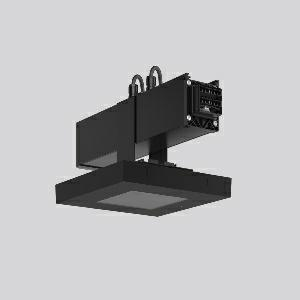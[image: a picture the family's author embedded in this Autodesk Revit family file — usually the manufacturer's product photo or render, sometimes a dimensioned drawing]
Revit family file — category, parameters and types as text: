
# Revit family: linedo_module_rt_9503rt_763_409_100_f551
name_source: partatom
category: Lighting Fixtures
units: mm (PartAtom-declared; Revit-internal decimal feet)

## family parameters
Cut with Voids When Loaded = No
Host = Face
Light Source = No
Part Type = Normal
Room Calculation Point = No
Round Connector Dimension = Use Diameter
Shared = No

## types (1)
- LINEDO Module RT (1 x LED Modul 765, 420 lm, 6500)
    Apparent Load = 7 VA
    CIE Flux Codes = 66 90 100 100 100
    Color Rendering = 70
    Color Temperature = 6500
    Default Elevation = 1800 mm
    Description = LINEDO, 6,7 W, 420 lm, 765, black, on/off
Continuous line luminaire, L 330 B 198 H 170, CBS, emergency-420 lm, AC-Control
    Height = 170 mm  [stored 0.557743 ft]
    Lamp = 1 x LED Modul 765
    Lamp Light Flux = 420 lm
    Lamp count = 1
    Length = 330 mm
    Lifetime = 50000 h
    Luminous efficacy = 63 lm/W
    Manufacturer = RZB
    ModVariant = No
    Model = 9503RT.763.409.100
    Mounting Place = Ceiling
    Mounting Type = Surface mounted, Pendant
    Number of Poles = 1
    OnlyDefault = Yes
    Power Factor = 1
    Product Name = LINEDO Module RT
    Product group = Continuous line luminaire system Linedo IP 54
    ProductGroupID = 314
    Protection Class = Protection class I
    Protection Degree = IP 54
    RLX_Detail_Level = 1
    RLX_Emergency_Light_Flux = 420 lm
    RLX_Emergency_Type = 3
    RLX_Emergency_Type_DB = Yes
    RlxData = <blob elided: 34857 chars, md5=db063a99>
    Socket = socket
    Standby Power = 0 W
    System Light Flux = 420 lm
    System Power = 7 W
    Type Comments = Product without accessories
    Type Image = 9503rw.763.434.000.jpg
    URL = http://relux.com
    VarID = ---
    Voltage = 230 V
    Voltage Range = 220-240 V
    Weight = 0.00 kg
    Width = 198 mm

note: [stored X ft] marks values corroborated as IEEE doubles in the binary element streams (Revit-internal decimal feet)

## geometry (parser evidence)
native form markers: Blend x4, Sweep x15
no freeform markers — native parametric forms only
